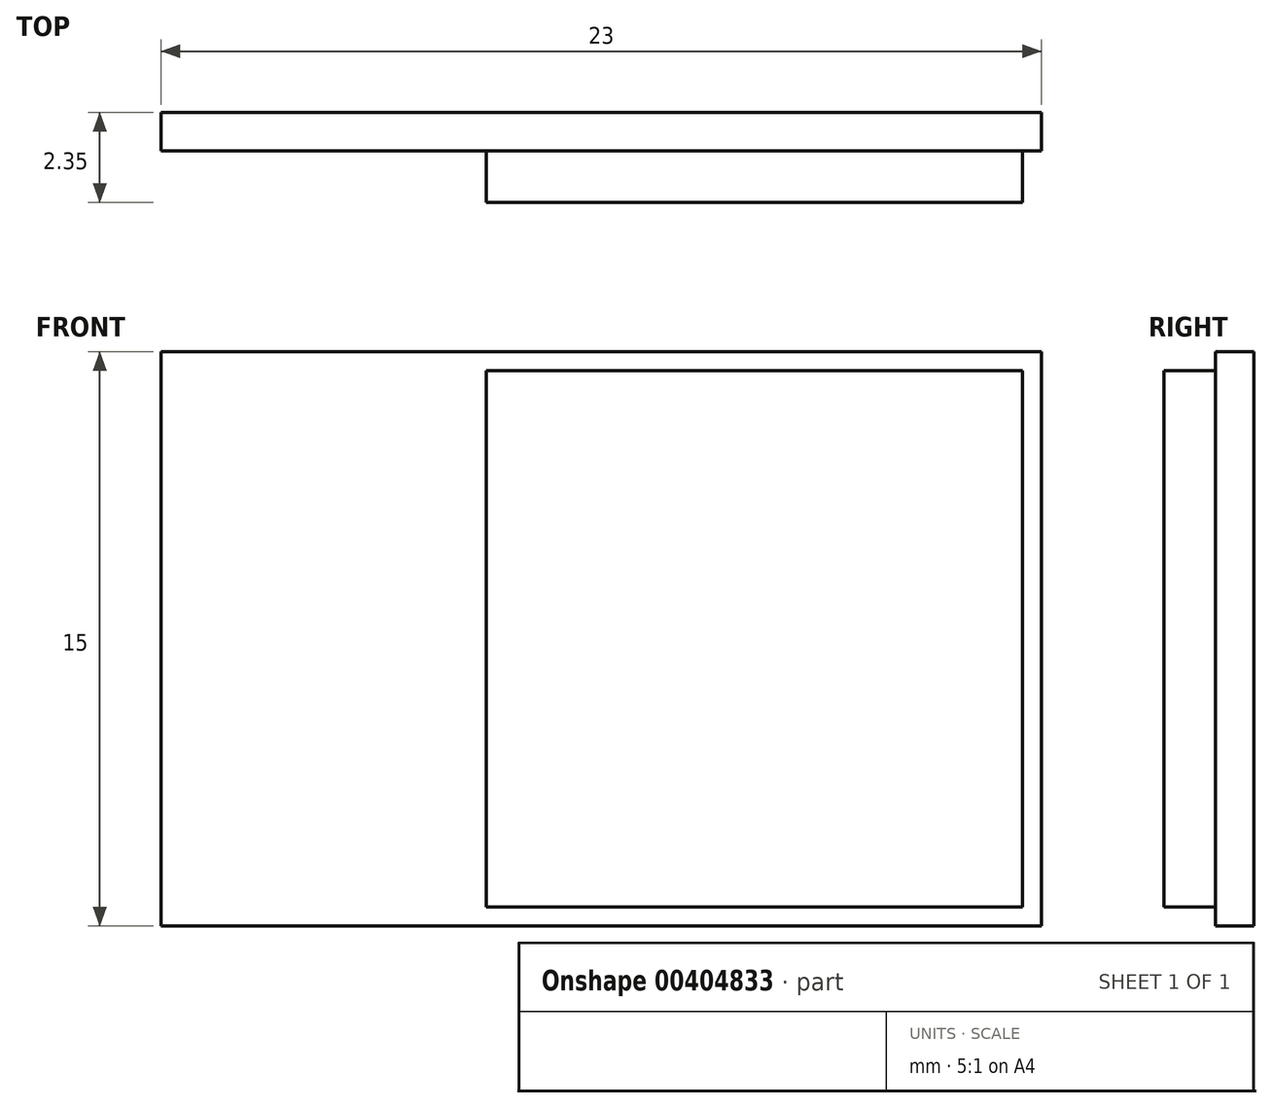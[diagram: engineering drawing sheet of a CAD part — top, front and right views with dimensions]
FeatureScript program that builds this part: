
annotation { "Feature Type Name" : "Feature", "Feature Type Description" : "" }
export const myFeature = defineFeature(function(context is Context, id is Id, definition is map)
    precondition{}
    {
        {
            var Q0;
            Q0=qCreatedBy(makeId("Front.planeOp"),FACE);
            var sketch = newSketch(context, id + "F0", { "sketchPlane" : qUnion([Q0])});
            skLineSegment(sketch, "E0", {"start": v(0, 15) * mm, "end": v(23, 15) * mm});
            skLineSegment(sketch, "E1", {"start": v(23, 15) * mm, "end": v(23, 0) * mm});
            skLineSegment(sketch, "E2", {"start": v(23, 0) * mm, "end": v(0, 0) * mm});
            skLineSegment(sketch, "E3", {"start": v(0, 0) * mm, "end": v(0, 15) * mm});
            skSolve(sketch);
        }
        {
            var Q0;
            Q0=makeQuery(id+"F0.imprint","IMPRINT",FACE,{"disambiguationData":[TD([[makeQuery(id+"F0.imprint","IMPRINT",EDGE,{"derivedFrom":sQuery(id+"F0.wireOp",EDGE,"E0")}),-1.0]])]});
            extrude(context, id + "F1", {"entities" : qUnion([Q0]), "depth" : 1 * mm});
        }
        {
            var Q0;
            Q0=makeQuery(id+"F1.opExtrude","CAP_FACE",FACE,{"disambiguationData":[OSD([sQuery(id+"F0.wireOp",EDGE,"E0"),sQuery(id+"F0.wireOp",EDGE,"E1"),sQuery(id+"F0.wireOp",EDGE,"E2"),sQuery(id+"F0.wireOp",EDGE,"E3")])],"isStart":false});
            var sketch = newSketch(context, id + "F2", { "sketchPlane" : qUnion([Q0])});
            skLineSegment(sketch, "E4.bottom", {"start": v(8.5, 14.5) * mm, "end": v(22.5, 14.5) * mm});
            skLineSegment(sketch, "E4.top", {"start": v(8.5, 0.5) * mm, "end": v(22.5, 0.5) * mm});
            skLineSegment(sketch, "E4.left", {"start": v(8.5, 14.5) * mm, "end": v(8.5, 0.5) * mm});
            skLineSegment(sketch, "E4.right", {"start": v(22.5, 14.5) * mm, "end": v(22.5, 0.5) * mm});
            skSolve(sketch);
        }
        {
            var Q0;
            Q0 = qSketchRegion(id + "F2", true);
            extrude(context, id + "F3", {"entities" : qUnion([Q0]), "operationType" : NewBodyOperationType.ADD, "depth" : 1.35 * mm});
        }
    });
